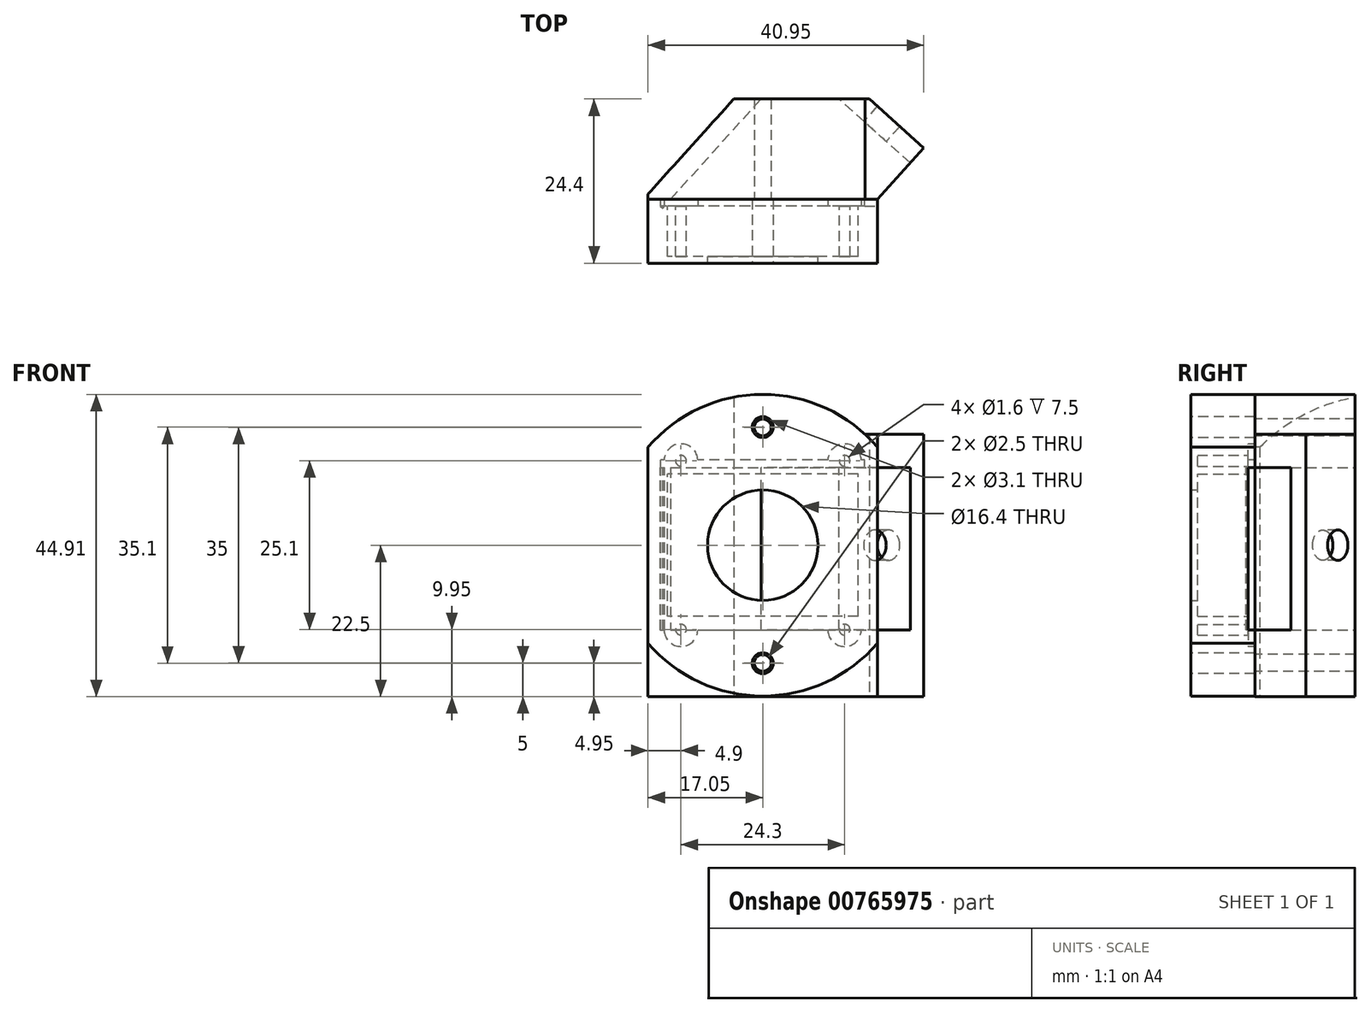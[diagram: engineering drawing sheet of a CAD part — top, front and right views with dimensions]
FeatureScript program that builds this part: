
annotation { "Feature Type Name" : "Feature", "Feature Type Description" : "" }
export const myFeature = defineFeature(function(context is Context, id is Id, definition is map)
    precondition{}
    {
        {
            var Q0;
            Q0=qCreatedBy(makeId("Front.planeOp"),FACE);
            var sketch = newSketch(context, id + "F0", { "sketchPlane" : qUnion([Q0])});
            skCircle(sketch, "E0", {"center": v(0, 0) * mm, "radius": 8 * mm});
            skLineSegment(sketch, "E1.bottom", {"start": v(15.05, -12.55) * mm, "end": v(-15.05, -12.55) * mm});
            skLineSegment(sketch, "E1.top", {"start": v(15.05, 12.55) * mm, "end": v(-15.05, 12.55) * mm});
            skLineSegment(sketch, "E1.left", {"start": v(15.05, -12.55) * mm, "end": v(15.05, 12.55) * mm});
            skLineSegment(sketch, "E1.right", {"start": v(-15.05, -12.55) * mm, "end": v(-15.05, 12.55) * mm});
            skCircle(sketch, "E2", {"center": v(-12.15, 12.55) * mm, "radius": 1 * mm});
            skCircle(sketch, "E3", {"center": v(12.15, 12.55) * mm, "radius": 1 * mm});
            skCircle(sketch, "E4", {"center": v(12.15, -12.55) * mm, "radius": 1 * mm});
            skCircle(sketch, "E5", {"center": v(-12.15, -12.55) * mm, "radius": 1 * mm});
            skLineSegment(sketch, "E6.bottom", {"start": v(12.15, 12.55) * mm, "end": v(-12.15, 12.55) * mm, "construction": true});
            skLineSegment(sketch, "E6.top", {"start": v(12.15, -12.55) * mm, "end": v(-12.15, -12.55) * mm, "construction": true});
            skLineSegment(sketch, "E6.left", {"start": v(12.15, 12.55) * mm, "end": v(12.15, -12.55) * mm, "construction": true});
            skLineSegment(sketch, "E6.right", {"start": v(-12.15, 12.55) * mm, "end": v(-12.15, -12.55) * mm, "construction": true});
            skSolve(sketch);
        }
        {
            assignVariable(context, id + "F1", {"variableType" : VariableType.LENGTH, "name" : "ChipDepth", "lengthValue" : 7.5 * mm});
        }
        {
            var Q0;
            Q0=qCreatedBy(makeId("Front.planeOp"),FACE);
            var sketch = newSketch(context, id + "F2", { "sketchPlane" : qUnion([Q0])});
            skLineSegment(sketch, "E7.bottom", {"start": v(17.05, -14.55) * mm, "end": v(-17.05, -14.55) * mm});
            skLineSegment(sketch, "E7.top", {"start": v(17.05, 14.55) * mm, "end": v(-17.05, 14.55) * mm});
            skLineSegment(sketch, "E7.left", {"start": v(17.05, -14.55) * mm, "end": v(17.05, 14.55) * mm});
            skLineSegment(sketch, "E7.right", {"start": v(-17.05, -14.55) * mm, "end": v(-17.05, 14.55) * mm});
            skPoint(sketch, "E7.middle", {"position": v(0, 0) * mm});
            skLineSegment(sketch, "E8.bottom", {"start": v(15.15, -12.65) * mm, "end": v(-15.15, -12.65) * mm});
            skLineSegment(sketch, "E8.top", {"start": v(15.15, 12.65) * mm, "end": v(-15.15, 12.65) * mm});
            skLineSegment(sketch, "E8.left", {"start": v(15.15, -12.65) * mm, "end": v(15.15, 12.65) * mm});
            skLineSegment(sketch, "E8.right", {"start": v(-15.15, -12.65) * mm, "end": v(-15.15, 12.65) * mm});
            skSolve(sketch);
        }
        {
            var Q0;
            Q0 = qSketchRegion(id + "F2", true);
            extrude(context, id + "F3", {"entities" : qUnion([Q0]), "depth" : getVariable(context, 'ChipDepth'), "offsetDistance" : 25 * mm, "hasSecondDirection" : true, "secondDirectionOppositeDirection" : true, "secondDirectionDepth" : 1 * mm});
        }
        {
            var Q0;
            Q0=makeQuery(id+"F3.opExtrude","CAP_FACE",FACE,{"disambiguationData":[OSD([sQuery(id+"F2.wireOp",EDGE,"E7.bottom"),sQuery(id+"F2.wireOp",EDGE,"E7.top"),sQuery(id+"F2.wireOp",EDGE,"E7.left"),sQuery(id+"F2.wireOp",EDGE,"E7.right"),sQuery(id+"F2.wireOp",EDGE,"E8.bottom"),sQuery(id+"F2.wireOp",EDGE,"E8.top"),sQuery(id+"F2.wireOp",EDGE,"E8.left"),sQuery(id+"F2.wireOp",EDGE,"E8.right")])],"isStart":false});
            var sketch = newSketch(context, id + "F4", { "sketchPlane" : qUnion([Q0])});
            skLineSegment(sketch, "E9.bottom", {"start": v(17.05, -14.55) * mm, "end": v(-17.05, -14.55) * mm});
            skLineSegment(sketch, "E9.top", {"start": v(17.05, 14.55) * mm, "end": v(-17.05, 14.55) * mm});
            skLineSegment(sketch, "E9.left", {"start": v(17.05, -14.55) * mm, "end": v(17.05, 14.55) * mm});
            skLineSegment(sketch, "E9.right", {"start": v(-17.05, -14.55) * mm, "end": v(-17.05, 14.55) * mm});
            skPoint(sketch, "E9.middle", {"position": v(0, 0) * mm});
            skCircle(sketch, "E10", {"center": v(0, 0) * mm, "radius": 8.2 * mm});
            skSolve(sketch);
        }
        {
            var Q0;
            Q0 = qSketchRegion(id + "F4", true);
            extrude(context, id + "F5", {"entities" : qUnion([Q0]), "operationType" : NewBodyOperationType.ADD, "depth" : 1 * mm, "offsetDistance" : 25 * mm});
        }
        {
            var Q0;
            Q0=qCreatedBy(makeId("Front.planeOp"),FACE);
            var sketch = newSketch(context, id + "F6", { "sketchPlane" : qUnion([Q0])});
            skLineSegment(sketch, "E11.bottom", {"start": v(15.15, -12.65) * mm, "end": v(-15.15, -12.65) * mm});
            skLineSegment(sketch, "E11.top", {"start": v(15.15, 12.65) * mm, "end": v(-15.15, 12.65) * mm});
            skLineSegment(sketch, "E11.left", {"start": v(15.15, -12.65) * mm, "end": v(15.15, 12.65) * mm});
            skLineSegment(sketch, "E11.right", {"start": v(-15.15, -12.65) * mm, "end": v(-15.15, 12.65) * mm});
            skPoint(sketch, "E11.middle", {"position": v(0, 0) * mm});
            skLineSegment(sketch, "E12.bottom", {"start": v(14.15, -10.55) * mm, "end": v(-14.15, -10.55) * mm});
            skLineSegment(sketch, "E12.top", {"start": v(14.15, 10.55) * mm, "end": v(-14.15, 10.55) * mm});
            skLineSegment(sketch, "E12.left", {"start": v(14.15, -10.55) * mm, "end": v(14.15, 10.55) * mm});
            skLineSegment(sketch, "E12.right", {"start": v(-14.15, -10.55) * mm, "end": v(-14.15, 10.55) * mm});
            skSolve(sketch);
        }
        {
            var Q0;
            Q0 = qSketchRegion(id + "F6", true);
            var Q1;
            Q1=makeQuery(id+"F5.opExtrude","CAP_FACE",FACE,{"disambiguationData":[OSD([sQuery(id+"F4.wireOp",EDGE,"E9.bottom"),sQuery(id+"F4.wireOp",EDGE,"E9.top"),sQuery(id+"F4.wireOp",EDGE,"E9.left"),sQuery(id+"F4.wireOp",EDGE,"E9.right"),sQuery(id+"F4.wireOp",EDGE,"E10")])],"isStart":true});
            extrude(context, id + "F7", {"entities" : qUnion([Q0]), "operationType" : NewBodyOperationType.ADD, "endBound" : BoundingType.UP_TO_SURFACE, "depth" : 25 * mm, "endBoundEntityFace" : qUnion([Q1]), "offsetDistance" : 25 * mm});
        }
        {
            var Q0;
            Q0=qCreatedBy(makeId("Front.planeOp"),FACE);
            var sketch = newSketch(context, id + "F8", { "sketchPlane" : qUnion([Q0])});
            skLineSegment(sketch, "E13", {"start": v(-17.05, 14.55) * mm, "end": v(17.05, 14.55) * mm});
            skLineSegment(sketch, "E14", {"start": v(17.05, -14.55) * mm, "end": v(-17.05, -14.55) * mm});
            skArc(sketch, "E15", {"start": v(-17.05, 14.55) * mm, "mid": v(0, 22.41) * mm, "end": v(17.05, 14.55) * mm});
            skArc(sketch, "E16", {"start": v(-17.05, -14.55) * mm, "mid": v(0, -22.41) * mm, "end": v(17.05, -14.55) * mm});
            skSolve(sketch);
        }
        {
            var Q0;
            Q0 = qSketchRegion(id + "F8", true);
            var Q1;
            Q1=makeQuery(id+"F5.opExtrude","CAP_FACE",FACE,{"disambiguationData":[OSD([sQuery(id+"F4.wireOp",EDGE,"E9.bottom"),sQuery(id+"F4.wireOp",EDGE,"E9.top"),sQuery(id+"F4.wireOp",EDGE,"E9.left"),sQuery(id+"F4.wireOp",EDGE,"E9.right"),sQuery(id+"F4.wireOp",EDGE,"E10")])],"isStart":false});
            var Q2;
            Q2=makeQuery(id+"F3.opExtrude","CAP_FACE",FACE,{"disambiguationData":[OSD([sQuery(id+"F2.wireOp",EDGE,"E7.bottom"),sQuery(id+"F2.wireOp",EDGE,"E7.top"),sQuery(id+"F2.wireOp",EDGE,"E7.left"),sQuery(id+"F2.wireOp",EDGE,"E7.right"),sQuery(id+"F2.wireOp",EDGE,"E8.bottom"),sQuery(id+"F2.wireOp",EDGE,"E8.top"),sQuery(id+"F2.wireOp",EDGE,"E8.left"),sQuery(id+"F2.wireOp",EDGE,"E8.right")])],"isStart":true});
            extrude(context, id + "F9", {"entities" : qUnion([Q0]), "operationType" : NewBodyOperationType.ADD, "endBound" : BoundingType.UP_TO_SURFACE, "depth" : 25 * mm, "endBoundEntityFace" : qUnion([Q1]), "offsetDistance" : 25 * mm, "hasSecondDirection" : true, "secondDirectionBound" : SecondDirectionBoundingType.UP_TO_SURFACE, "secondDirectionOppositeDirection" : true, "secondDirectionDepth" : 25 * mm, "secondDirectionBoundEntityFace" : qUnion([Q2])});
        }
        {
            var Q0;
            Q0=qCreatedBy(makeId("Front.planeOp"),FACE);
            var sketch = newSketch(context, id + "F10", { "sketchPlane" : qUnion([Q0])});
            skCircle(sketch, "E17", {"center": v(0, 17.55) * mm, "radius": 1.55 * mm});
            skCircle(sketch, "E18", {"center": v(0, -17.55) * mm, "radius": 1.55 * mm});
            skSolve(sketch);
        }
        {
            var Q0;
            Q0 = qSketchRegion(id + "F10", true);
            extrude(context, id + "F11", {"entities" : qUnion([Q0]), "operationType" : NewBodyOperationType.REMOVE, "endBound" : BoundingType.THROUGH_ALL, "oppositeDirection" : true, "depth" : 25 * mm, "offsetDistance" : 25 * mm, "hasSecondDirection" : true, "secondDirectionBound" : SecondDirectionBoundingType.THROUGH_ALL, "secondDirectionOppositeDirection" : false, "secondDirectionDepth" : 5 * mm});
        }
        {
            var Q0;
            Q0=makeQuery(id+"F0.imprint","IMPRINT",FACE,{"disambiguationData":[TD([[makeQuery(id+"F0.imprint","IMPRINT",EDGE,{"derivedFrom":sQuery(id+"F0.wireOp",EDGE,"E0")}),-1.0]])]});
            var sketch = newSketch(context, id + "F12", { "sketchPlane" : qUnion([Q0])});
            skCircle(sketch, "E19", {"center": v(12.15, 12.55) * mm, "radius": 2.5 * mm});
            skCircle(sketch, "E20", {"center": v(-12.15, 12.55) * mm, "radius": 2.5 * mm});
            skCircle(sketch, "E21", {"center": v(-12.15, -12.55) * mm, "radius": 2.5 * mm});
            skLineSegment(sketch, "E22.bottom", {"start": v(-12.15, 12.55) * mm, "end": v(12.15, 12.55) * mm, "construction": true});
            skLineSegment(sketch, "E22.top", {"start": v(-12.15, -12.55) * mm, "end": v(12.15, -12.55) * mm, "construction": true});
            skLineSegment(sketch, "E22.left", {"start": v(-12.15, 12.55) * mm, "end": v(-12.15, -12.55) * mm, "construction": true});
            skLineSegment(sketch, "E22.right", {"start": v(12.15, 12.55) * mm, "end": v(12.15, -12.55) * mm, "construction": true});
            skPoint(sketch, "E22.middle", {"position": v(0, 0) * mm});
            skCircle(sketch, "E23", {"center": v(12.15, -12.55) * mm, "radius": 2.5 * mm});
            skSolve(sketch);
        }
        {
            var Q0;
            Q0 = qSketchRegion(id + "F12", true);
            extrude(context, id + "F13", {"entities" : qUnion([Q0]), "operationType" : NewBodyOperationType.REMOVE, "oppositeDirection" : true, "depth" : 25 * mm, "offsetDistance" : 25 * mm});
        }
        {
            var Q0;
            Q0=qCreatedBy(makeId("Front.planeOp"),FACE);
            var sketch = newSketch(context, id + "F14", { "sketchPlane" : qUnion([Q0])});
            skLineSegment(sketch, "E24.bottom", {"start": v(-12.15, 12.55) * mm, "end": v(12.15, 12.55) * mm, "construction": true});
            skLineSegment(sketch, "E24.top", {"start": v(-12.15, -12.55) * mm, "end": v(12.15, -12.55) * mm, "construction": true});
            skLineSegment(sketch, "E24.left", {"start": v(-12.15, 12.55) * mm, "end": v(-12.15, -12.55) * mm, "construction": true});
            skLineSegment(sketch, "E24.right", {"start": v(12.15, 12.55) * mm, "end": v(12.15, -12.55) * mm, "construction": true});
            skPoint(sketch, "E24.middle", {"position": v(0, 0) * mm});
            skCircle(sketch, "E25", {"center": v(12.15, 12.55) * mm, "radius": 0.8 * mm});
            skCircle(sketch, "E26", {"center": v(-12.15, 12.55) * mm, "radius": 0.8 * mm});
            skCircle(sketch, "E27", {"center": v(-12.15, -12.55) * mm, "radius": 0.8 * mm});
            skCircle(sketch, "E28", {"center": v(12.15, -12.55) * mm, "radius": 0.8 * mm});
            skSolve(sketch);
        }
        {
            var Q0;
            Q0 = qSketchRegion(id + "F14", true);
            var Q1;
            Q1=makeQuery(id+"F5.opExtrude","CAP_FACE",FACE,{"disambiguationData":[OSD([sQuery(id+"F4.wireOp",EDGE,"E9.bottom"),sQuery(id+"F4.wireOp",EDGE,"E9.top"),sQuery(id+"F4.wireOp",EDGE,"E9.left"),sQuery(id+"F4.wireOp",EDGE,"E9.right"),sQuery(id+"F4.wireOp",EDGE,"E10")])],"isStart":true});
            extrude(context, id + "F15", {"entities" : qUnion([Q0]), "operationType" : NewBodyOperationType.REMOVE, "endBound" : BoundingType.UP_TO_SURFACE, "depth" : 25 * mm, "endBoundEntityFace" : qUnion([Q1]), "offsetDistance" : 25 * mm});
        }
        {
            var Q0;
            Q0=qCreatedBy(makeId("Top.planeOp"),FACE);
            var sketch = newSketch(context, id + "F16", { "sketchPlane" : qUnion([Q0])});
            skLineSegment(sketch, "E29", {"start": v(25.73, 6.96) * mm, "end": v(4.7, 25.9) * mm});
            skLineSegment(sketch, "E30", {"start": v(4.7, 25.9) * mm, "end": v(-27.32, -9.66) * mm});
            skLineSegment(sketch, "E31", {"start": v(18.67, 13.32) * mm, "end": v(14.12, 8.27) * mm, "construction": true});
            skLineSegment(sketch, "E32", {"start": v(17.18, 14.66) * mm, "end": v(12.63, 9.6) * mm});
            skLineSegment(sketch, "E33", {"start": v(12.63, 9.6) * mm, "end": v(15.6, 6.93) * mm});
            skLineSegment(sketch, "E34", {"start": v(15.6, 6.93) * mm, "end": v(20.16, 11.98) * mm});
            skLineSegment(sketch, "E35", {"start": v(-2.12, -46.68) * mm, "end": v(-149.33, -210.17) * mm});
            skLineSegment(sketch, "E36", {"start": v(-2.12, -46.68) * mm, "end": v(161.37, -193.89) * mm});
            skPoint(sketch, "E37", {"position": v(-18.62, 0) * mm});
            skLineSegment(sketch, "E38", {"start": v(-149.33, -210.17) * mm, "end": v(14.16, -357.38) * mm});
            skLineSegment(sketch, "E39", {"start": v(14.16, -357.38) * mm, "end": v(161.37, -193.89) * mm});
            skLineSegment(sketch, "E40", {"start": v(0, -208.72) * mm, "end": v(0, 0) * mm, "construction": true});
            skPoint(sketch, "E41", {"position": v(0, -208.72) * mm});
            skLineSegment(sketch, "E42", {"start": v(-141.23, -216.12) * mm, "end": v(-7.4, -67.5) * mm, "construction": true});
            skLineSegment(sketch, "E43", {"start": v(-7.4, -67.5) * mm, "end": v(141.23, -201.32) * mm, "construction": true});
            skLineSegment(sketch, "E44", {"start": v(141.23, -201.32) * mm, "end": v(7.4, -349.95) * mm, "construction": true});
            skLineSegment(sketch, "E45", {"start": v(7.4, -349.95) * mm, "end": v(-141.23, -216.12) * mm, "construction": true});
            skLineSegment(sketch, "E46", {"start": v(-141.23, -216.12) * mm, "end": v(141.23, -201.32) * mm, "construction": true});
            skLineSegment(sketch, "E47.bottom", {"start": v(8, -8.5) * mm, "end": v(-8, -8.5) * mm, "construction": true});
            skLineSegment(sketch, "E47.top", {"start": v(8, -28.5) * mm, "end": v(-8, -28.5) * mm, "construction": true});
            skLineSegment(sketch, "E47.left", {"start": v(8, -8.5) * mm, "end": v(8, -28.5) * mm, "construction": true});
            skLineSegment(sketch, "E47.right", {"start": v(-8, -8.5) * mm, "end": v(-8, -28.5) * mm, "construction": true});
            skPoint(sketch, "E47.middle", {"position": v(0, -18.5) * mm});
            skSolve(sketch);
        }
        {
            var Q0;
            Q0=qCreatedBy(makeId("Top.planeOp"),FACE);
            var sketch = newSketch(context, id + "F17", { "sketchPlane" : qUnion([Q0])});
            skLineSegment(sketch, "E48", {"start": v(-4.3, 15.9) * mm, "end": v(15.8, 15.9) * mm});
            skLineSegment(sketch, "E49", {"start": v(17.05, 1) * mm, "end": v(23.9, 8.6) * mm});
            skLineSegment(sketch, "E50", {"start": v(23.9, 8.6) * mm, "end": v(15.8, 15.9) * mm});
            skLineSegment(sketch, "E51", {"start": v(-17.05, 1) * mm, "end": v(-17.05, 1.75) * mm});
            skLineSegment(sketch, "E52", {"start": v(-17.05, 1.75) * mm, "end": v(-4.3, 15.9) * mm});
            skLineSegment(sketch, "E53", {"start": v(-17.05, 1) * mm, "end": v(17.05, 1) * mm});
            skSolve(sketch);
        }
        {
            var Q0;
            Q0 = qSketchRegion(id + "F17", true);
            extrude(context, id + "F18", {"entities" : qUnion([Q0]), "endBound" : BoundingType.SYMMETRIC, "depth" : 45 * mm, "offsetDistance" : 25 * mm});
        }
        {
            var Q0;
            Q0=qCreatedBy(makeId("Top.planeOp"),FACE);
            var sketch = newSketch(context, id + "F19", { "sketchPlane" : qUnion([Q0])});
            skLineSegment(sketch, "E54", {"start": v(28.98, 0) * mm, "end": v(11.32, 15.9) * mm});
            skLineSegment(sketch, "E55", {"start": v(11.32, 15.9) * mm, "end": v(-0.27, 15.9) * mm});
            skLineSegment(sketch, "E56", {"start": v(-14.87, -0.31) * mm, "end": v(-0.27, 15.9) * mm});
            skLineSegment(sketch, "E57", {"start": v(-11, 3.99) * mm, "end": v(-13.23, 6) * mm, "construction": true});
            skLineSegment(sketch, "E58", {"start": v(19.09, 8.9) * mm, "end": v(21.1, 11.14) * mm, "construction": true});
            skLineSegment(sketch, "E59", {"start": v(-15.22, 0) * mm, "end": v(-14.87, -0.31) * mm});
            skLineSegment(sketch, "E60", {"start": v(-15.22, 0) * mm, "end": v(28.98, 0) * mm});
            skLineSegment(sketch, "E61", {"start": v(-15.04, -0.16) * mm, "end": v(-17.05, -2.39) * mm, "construction": true});
            skSolve(sketch);
        }
        {
            var Q0;
            Q0 = qSketchRegion(id + "F19", true);
            extrude(context, id + "F20", {"entities" : qUnion([Q0]), "operationType" : NewBodyOperationType.REMOVE, "oppositeDirection" : true, "depth" : 12.6 * mm, "offsetDistance" : 25 * mm, "hasSecondDirection" : true, "secondDirectionOppositeDirection" : false, "secondDirectionDepth" : 11.5 * mm});
        }
        {
            var Q0;
            Q0=makeQuery(id+"F20.boolean.opBoolean","COPY",FACE,{"derivedFrom":makeQuery(id+"F20.opExtrude","SWEPT_FACE",FACE,{"disambiguationData":[OSD([sQuery(id+"F19.wireOp",EDGE,"E54")])]})});
            var sketch = newSketch(context, id + "F21", { "sketchPlane" : qUnion([Q0])});
            skCircle(sketch, "E62", {"center": v(4.96, 0) * mm, "radius": 2.25 * mm});
            skSolve(sketch);
        }
        {
            var Q0;
            Q0 = qSketchRegion(id + "F21", true);
            extrude(context, id + "F22", {"entities" : qUnion([Q0]), "operationType" : NewBodyOperationType.REMOVE, "endBound" : BoundingType.THROUGH_ALL, "oppositeDirection" : true, "depth" : 25 * mm, "offsetDistance" : 25 * mm});
        }
        {
            var Q0;
            Q0=qCreatedBy(makeId("Front.planeOp"),FACE);
            var sketch = newSketch(context, id + "F23", { "sketchPlane" : qUnion([Q0])});
            skCircle(sketch, "E63", {"center": v(0, 17.5) * mm, "radius": 1.25 * mm});
            skCircle(sketch, "E64", {"center": v(0, -17.5) * mm, "radius": 1.25 * mm});
            skSolve(sketch);
        }
        {
            var Q0;
            Q0 = qSketchRegion(id + "F23", true);
            extrude(context, id + "F24", {"entities" : qUnion([Q0]), "operationType" : NewBodyOperationType.REMOVE, "endBound" : BoundingType.THROUGH_ALL, "oppositeDirection" : true, "depth" : 25 * mm, "offsetDistance" : 25 * mm});
        }
        {
            var Q0;
            Q0=qCreatedBy(makeId("Front.planeOp"),FACE);
            var sketch = newSketch(context, id + "F25", { "sketchPlane" : qUnion([Q0])});
            skArc(sketch, "E65", {"start": v(-21, 7.85) * mm, "mid": v(-5.21, 21.8) * mm, "end": v(15.17, 16.5) * mm});
            skLineSegment(sketch, "E66", {"start": v(-21, 7.85) * mm, "end": v(-21, 29.14) * mm});
            skLineSegment(sketch, "E67", {"start": v(-21, 29.14) * mm, "end": v(34.97, 29.14) * mm});
            skLineSegment(sketch, "E68", {"start": v(15.17, 16.5) * mm, "end": v(34.97, 16.5) * mm});
            skLineSegment(sketch, "E69", {"start": v(34.97, 16.5) * mm, "end": v(34.97, 29.14) * mm});
            skSolve(sketch);
        }
        {
            var Q0;
            Q0 = qSketchRegion(id + "F25", true);
            extrude(context, id + "F26", {"entities" : qUnion([Q0]), "operationType" : NewBodyOperationType.REMOVE, "endBound" : BoundingType.THROUGH_ALL, "oppositeDirection" : true, "depth" : 25 * mm, "offsetDistance" : 25 * mm});
        }
    });
